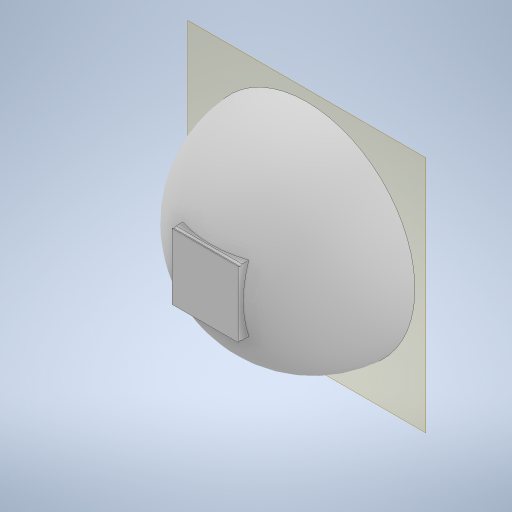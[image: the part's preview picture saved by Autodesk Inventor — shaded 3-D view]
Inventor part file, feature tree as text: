
AUTODESK INVENTOR PART (.ipt)
format: ipt  version: 2023.2 (Build 272271000, 271)  size: 304,128 bytes
history: native  units: mm
features: sketch x4, extrude x3, plane x2, revolve x1, shell x1
ambient origin geometry x8: Origin, YZ Plane, XZ Plane, XY Plane, X Axis, Y Axis, Z Axis, Center Point
bodies: Volumenkörper1 (feature_tree)
feature tree (11):
  revolve  "Umdrehung1"
  plane  "Arbeitsebene1"
  extrude  "Extrusion1"  TaperAngle=360.0deg  [1 undecoded]
  shell  "Wandung1"  Thickness=5.0mm
  plane  "Arbeitsebene2"
  extrude  "Extrusion2"  Depth=0.8mm
  extrude  "Extrusion3"  Depth=50.0mm
  sketch  "Skizze1"  dims[d0=164.0mm d1=360.0deg d2=5.0mm]
  sketch  "Skizze2"  dims[d3=0.0mm d4=0.0mm d5=0.8mm]
  sketch  "Skizze3"  dims[d6=82.0mm d7=50.0mm]
  sketch  "Skizze4"  dims[d8=50.0mm d9=10.0mm d10=0.0mm d12=30.0deg d13=1.5mm d14=0.0mm d15=0.0mm]
note: 1 required parameter value undecoded (feature->parameter linkage not recoverable at this tier; creation-order binding heuristic only, values carry confidence <= 0.55)
